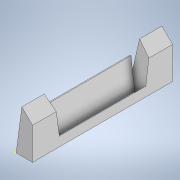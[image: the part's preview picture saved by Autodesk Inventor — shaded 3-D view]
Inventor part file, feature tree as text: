
AUTODESK INVENTOR PART (.ipt)
format: ipt  version: 2021 (Build 250183000, 183)  size: 207,360 bytes
history: native  units: in
note: dims shown in document units (in); Inventor stores cm internally (conversion verified against a paired STEP export)
features: extrude x7, sketch x7, projected_geometry x5
ambient origin geometry x8: Origin, YZ Plane, XZ Plane, XY Plane, X Axis, Y Axis, Z Axis, Center Point
bodies: Solid1 (feature_tree)
feature tree (19):
  extrude  "Extrusion1"  Depth=0.2362in
  extrude  "Extrusion2"  Depth=0.378in
  extrude  "Extrusion3"  Depth=0.1181in
  extrude  "Extrusion4"  Depth=0.378in TaperAngle=0.0deg
  extrude  "Extrusion5"  Depth=0.9188in TaperAngle=0.0deg
  extrude  "Extrusion6"  Depth=0.8312in TaperAngle=0.0deg
  extrude  "Extrusion7"  Depth=0.0236in
  sketch  "Sketch12"  dims[d27=0.1575in d28=0.0394in d29=0.0079in d30=0.0079in d31=0.0079in d38=0.0157in d40=0.0787in d44=0.0079in d45=0.0079in d46=0.5906in d47=0.0787in d48=0.0079in d49=0.0236in]
  sketch  "Sketch1"  dims[d0=0.2362in d3=0.4331in]
  sketch  "Sketch2"  dims[d4=0.378in d5=0.0in d6=0.1181in]
  sketch  "Sketch3"  dims[d7=0.4331in d8=0.1181in]
  projected_geometry  "Projected Loop1"
  sketch  "Sketch5"  dims[d9=1.1339in d10=0.0in d11=0.378in d12=0.0in]
  sketch  "Sketch6"  dims[d16=0.9188in d17=0.0in d18=0.9188in d19=0.0in]
  sketch  "Sketch7"  dims[d21=0.8312in d22=0.0in d23=0.8312in d24=0.0in]
  projected_geometry  "Projected Loop11"
  projected_geometry  "Projected Loop12"
  projected_geometry  "Projected Loop13"
  projected_geometry  "Projected Loop14"
